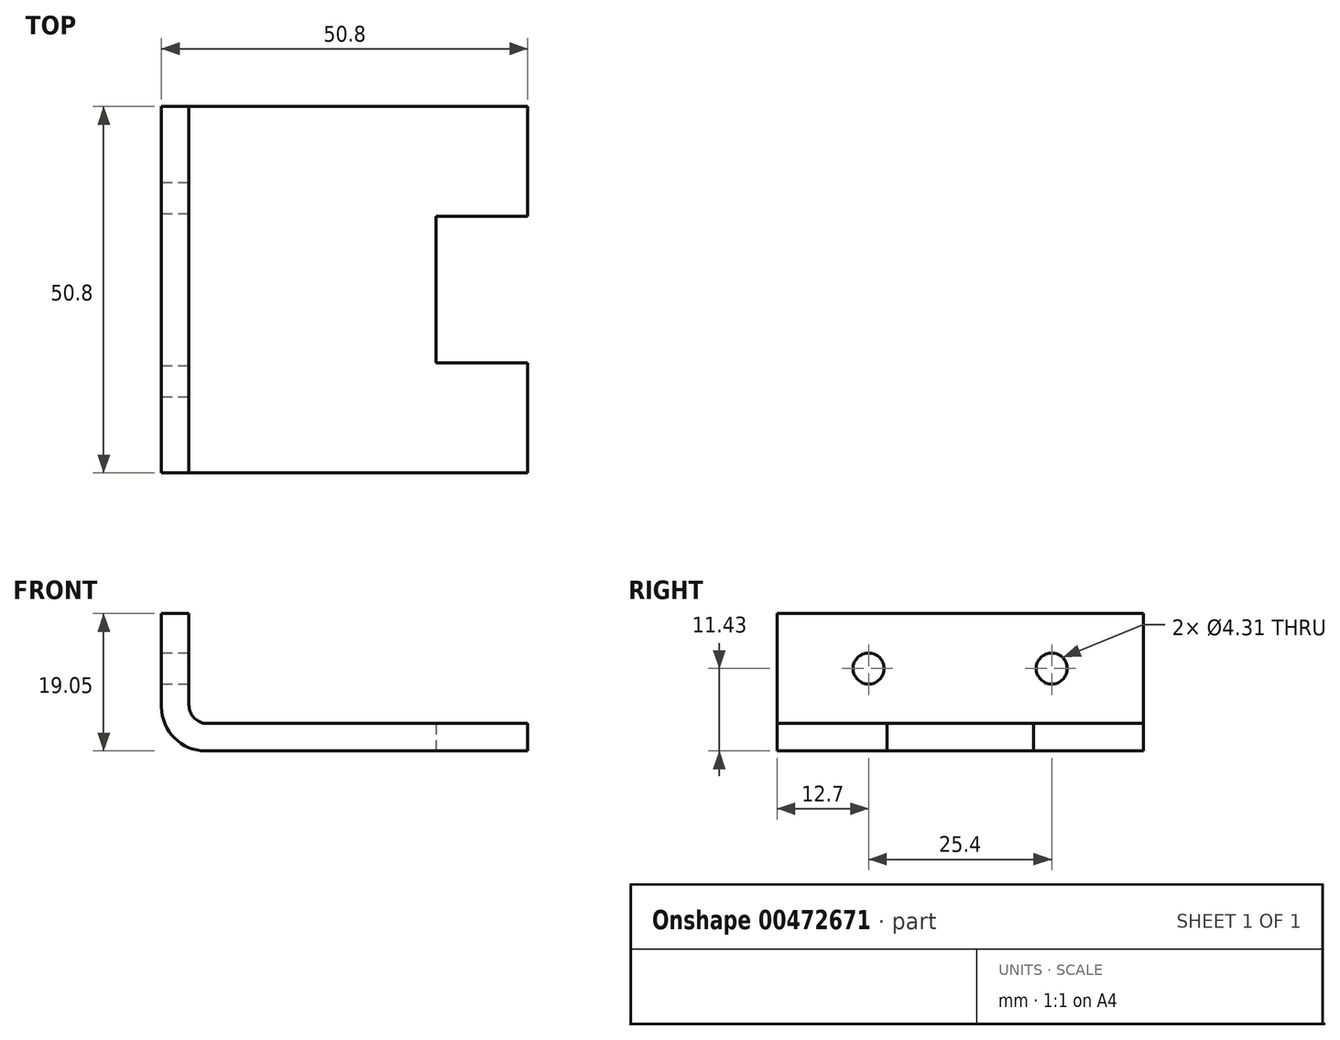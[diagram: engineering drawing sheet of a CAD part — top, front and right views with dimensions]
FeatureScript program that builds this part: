
annotation { "Feature Type Name" : "Feature", "Feature Type Description" : "" }
export const myFeature = defineFeature(function(context is Context, id is Id, definition is map)
    precondition{}
    {
        {
            var Q0;
            Q0=qCreatedBy(makeId("Top.planeOp"),FACE);
            var sketch = newSketch(context, id + "F0", { "sketchPlane" : qUnion([Q0])});
            skLineSegment(sketch, "E0", {"start": v(38.1, 35.56) * mm, "end": v(38.1, 15.24) * mm});
            skLineSegment(sketch, "E1", {"start": v(38.1, 15.24) * mm, "end": v(50.8, 15.24) * mm});
            skLineSegment(sketch, "E2", {"start": v(50.8, 15.24) * mm, "end": v(50.8, 0) * mm});
            skLineSegment(sketch, "E3", {"start": v(50.8, 0) * mm, "end": v(0, 0) * mm});
            skLineSegment(sketch, "E4", {"start": v(0, 0) * mm, "end": v(0, 50.8) * mm});
            skLineSegment(sketch, "E5", {"start": v(0, 50.8) * mm, "end": v(50.8, 50.8) * mm});
            skLineSegment(sketch, "E6", {"start": v(50.8, 50.8) * mm, "end": v(50.8, 35.56) * mm});
            skLineSegment(sketch, "E7", {"start": v(50.8, 35.56) * mm, "end": v(38.1, 35.56) * mm});
            skSolve(sketch);
        }
        {
            var Q0;
            Q0 = qSketchRegion(id + "F0", true);
            extrude(context, id + "F1", {"entities" : qUnion([Q0]), "depth" : 19.05 * mm, "offsetDistance" : 25.4 * mm});
        }
        {
            var Q0;
            Q0=makeQuery(id+"F1.opExtrude","SWEPT_FACE",FACE,{"disambiguationData":[OSD([sQuery(id+"F0.wireOp",EDGE,"E5")])]});
            var sketch = newSketch(context, id + "F2", { "sketchPlane" : qUnion([Q0])});
            skLineSegment(sketch, "E8.bottom", {"start": v(-50.8, 19.05) * mm, "end": v(-3.81, 19.05) * mm});
            skLineSegment(sketch, "E8.top", {"start": v(-50.8, 3.8) * mm, "end": v(-3.81, 3.81) * mm});
            skLineSegment(sketch, "E8.left", {"start": v(-50.8, 19.05) * mm, "end": v(-50.8, 3.8) * mm});
            skLineSegment(sketch, "E8.right", {"start": v(-3.81, 19.05) * mm, "end": v(-3.81, 3.81) * mm});
            skSolve(sketch);
        }
        {
            var Q0;
            Q0 = qSketchRegion(id + "F2", true);
            extrude(context, id + "F3", {"entities" : qUnion([Q0]), "operationType" : NewBodyOperationType.REMOVE, "endBound" : BoundingType.THROUGH_ALL, "oppositeDirection" : true, "depth" : 25.4 * mm, "offsetDistance" : 25.4 * mm});
        }
        {
            var Q0;
            Q0=makeQuery(id+"F3.boolean.opBoolean","COPY",FACE,{"derivedFrom":makeQuery(id+"F3.opExtrude","SWEPT_FACE",FACE,{"disambiguationData":[OSD([sQuery(id+"F2.wireOp",EDGE,"E8.right")])]})});
            var sketch = newSketch(context, id + "F4", { "sketchPlane" : qUnion([Q0])});
            skCircle(sketch, "E9", {"center": v(38.1, 11.43) * mm, "radius": 2.15 * mm});
            skLineSegment(sketch, "E10", {"start": v(25.4, 3.81) * mm, "end": v(25.4, 19.05) * mm, "construction": true});
            skCircle(sketch, "E11.MirrorC", {"center": v(12.7, 11.43) * mm, "radius": 2.15 * mm});
            skLineSegment(sketch, "E12", {"start": v(38.1, 11.43) * mm, "end": v(50.8, 11.43) * mm, "construction": true});
            skSolve(sketch);
        }
        {
            var Q0;
            Q0 = qSketchRegion(id + "F4", true);
            extrude(context, id + "F5", {"entities" : qUnion([Q0]), "operationType" : NewBodyOperationType.REMOVE, "endBound" : BoundingType.THROUGH_ALL, "oppositeDirection" : true, "depth" : 25.4 * mm, "offsetDistance" : 25.4 * mm});
        }
        {
            var Q0;
            Q0=makeQuery(id+"F3.boolean.opBoolean","COPY",EDGE,{"derivedFrom":makeQuery(id+"F3.opExtrude","SWEPT_EDGE",EDGE,{"disambiguationData":[OSD([sQuery(id+"F2.wireOp",EDGE,"E8.top"),sQuery(id+"F2.wireOp",EDGE,"E8.right")])]})});
            fillet(context, id + "F6", {"entities" : qUnion([Q0]), "radius" : 2.54 * mm, "tangentPropagation" : true, "allowEdgeOverflow" : false});
        }
        {
            var Q0;
            Q0=makeQuery(id+"F1.opExtrude","CAP_EDGE",EDGE,{"disambiguationData":[OSD([sQuery(id+"F0.wireOp",EDGE,"E4")])],"isStart":true});
            fillet(context, id + "F7", {"entities" : qUnion([Q0]), "radius" : 6.13 * mm, "tangentPropagation" : true, "allowEdgeOverflow" : false});
        }
    });
